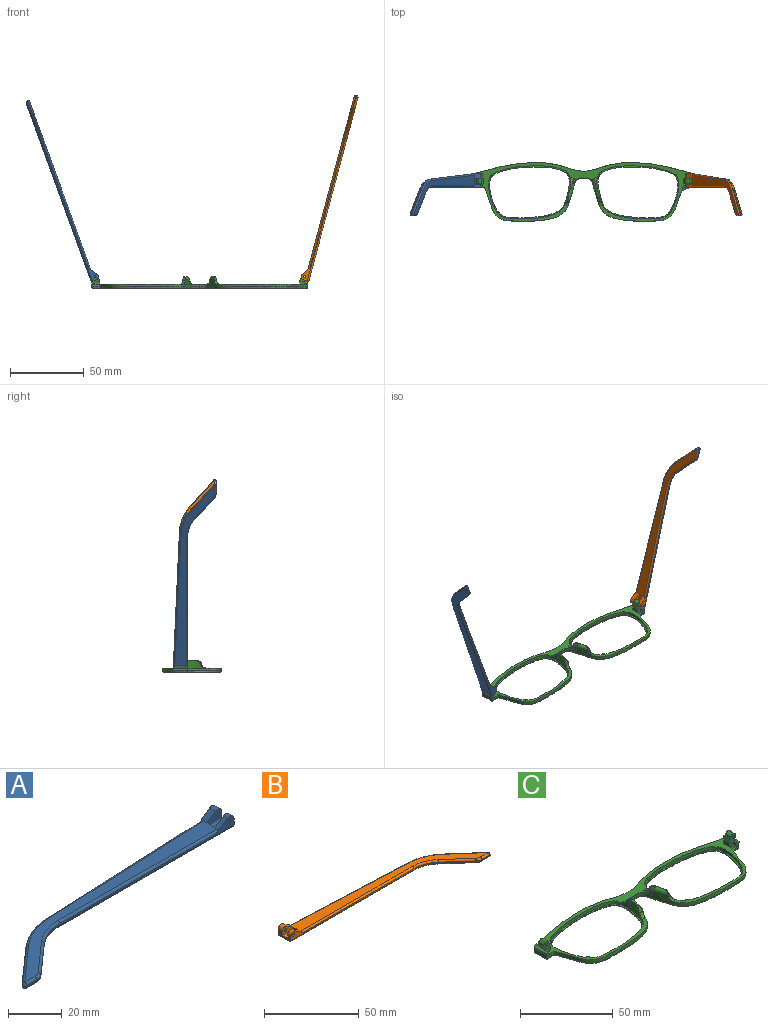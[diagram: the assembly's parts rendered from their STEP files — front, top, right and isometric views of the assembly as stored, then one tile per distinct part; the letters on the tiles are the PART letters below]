
ASSEMBLY  parts=3 mates=2
PART A: 43 faces, bbox 130.2x29.5x5.9 mm
  f0: plane 9.62x3.72mm, normal (1,0,0), area 24.7mm2, adj f1,f3,f4,f5,f10,f16,f18,f28
  f1: cylinder r=2.2mm len=3.45mm, axis (0,-1,0), area 11mm2, adj f0,f2,f4,f37
  f2: plane 6.01x3.91mm, normal (-0.55,0,0.84), area 12.7mm2, adj f1,f4,f9,f19,f37
  f3: plane 2.26x0.1mm, normal (0,0,1), area 0.1mm2, adj f0,f5,f18
  f4: plane 92.1x4.9mm, normal (0,-1,0), area 79.9mm2, adj f0,f1,f2,f14,f19,f36,f42
  f5: plane 93.42x4.13mm, normal (-0.04,1,0), area 64.8mm2, adj f0,f3,f11,f15,f17,f27,f28
  f6: plane 17.82x15.72mm, normal (-0.66,0.75,0), area 14.3mm2, adj f11,f12,f25,f30
  f7: plane 5.46x0.6mm, normal (0,-1,0), area 3.3mm2, adj f12,f13,f23,f32
  f8: plane 14.99x13.23mm, normal (0.66,-0.75,0), area 12mm2, adj f13,f14,f21,f34
  f9: plane 121.18x26.73mm, normal (0,0,1), area 627.7mm2, adj f2,f17,f19,f20,f21,f22,f23,f25
  f10: plane 129.1x27.08mm, normal (0,0,-1), area 686.5mm2, adj f0,f28,f29,f30,f32,f33,f34,f35
  f11: cylinder r=30mm len=18.52mm, axis (0,0,-1), area 12.2mm2, adj f5,f6,f26,f29
  f12: cylinder r=1mm len=1.75mm, axis (0,0,-1), area 1.5mm2, adj f6,f7,f24,f31
  f13: cylinder r=5mm len=3.31mm, axis (0,0,-1), area 2.2mm2, adj f7,f8,f22,f33
  f14: cylinder r=20mm len=13.23mm, axis (0,0,1), area 8.7mm2, adj f4,f8,f20,f35
  f15: plane 5.66x0.25mm, normal (0,0,-1), area 0.7mm2, adj f5,f17,f18
  f16: cylinder r=2.2mm len=3.45mm, axis (0,-1,0), area 14.8mm2, adj f0,f17,f18,f38
  f17: plane 6.01x3.91mm, normal (-0.55,0,0.84), area 16.9mm2, adj f5,f9,f15,f16,f18,f27,f38
  f18: plane 7.92x3.3mm, normal (0,1,0), area 15.9mm2, adj f0,f3,f15,f16,f17,f41
  f19: cylinder r=1mm len=84.18mm, axis (-1,0,0), area 131.4mm2, adj f2,f4,f9,f20
  f20: torus R=21mm, axis (0,0,1), area 23.1mm2, adj f9,f14,f19,f21
  f21: cylinder r=1mm len=15.65mm, axis (-0.75,-0.66,0), area 31.4mm2, adj f8,f9,f20,f22
  f22: torus R=4mm, axis (0,0,1), area 5.3mm2, adj f9,f13,f21,f23
  f23: cylinder r=1mm len=5.46mm, axis (-1,0,0), area 8.6mm2, adj f7,f9,f22,f24
  f24: sphere r=1mm, area 2.4mm2, adj f12,f23,f25
  f25: cylinder r=1mm len=18.48mm, axis (0.75,0.66,0), area 37.3mm2, adj f6,f9,f24,f26
  f26: torus R=29mm, axis (0,0,1), area 31.6mm2, adj f9,f11,f25,f27
  f27: cylinder r=1mm len=85.5mm, axis (1,0.04,0), area 133.5mm2, adj f5,f9,f17,f26
  f28: cylinder r=1mm len=93.46mm, axis (-1,-0.04,0), area 146.9mm2, adj f0,f5,f10,f29
  f29: torus R=29mm, axis (0,0,1), area 31.6mm2, adj f10,f11,f28,f30
  f30: cylinder r=1mm len=18.48mm, axis (-0.75,-0.66,0), area 37.3mm2, adj f6,f10,f29,f31
  f31: sphere r=1mm, area 2.4mm2, adj f12,f30,f32
  f32: cylinder r=1mm len=5.46mm, axis (1,0,0), area 8.6mm2, adj f7,f10,f31,f33
  f33: torus R=4mm, axis (0,0,1), area 5.3mm2, adj f10,f13,f32,f34
  f34: cylinder r=1mm len=15.65mm, axis (0.75,0.66,0), area 31.4mm2, adj f8,f10,f33,f35
  f35: torus R=21mm, axis (0,0,1), area 23.1mm2, adj f10,f14,f34,f36
  f36: cylinder r=1mm len=92.1mm, axis (1,0,0), area 144.7mm2, adj f0,f4,f10,f35
  f37: plane 7.92x4.7mm, normal (0,1,0), area 27mm2, adj f0,f1,f2,f39,f40,f42
  f38: plane 7.92x4.7mm, normal (0,-1,0), area 27mm2, adj f0,f16,f17,f39,f40,f41
  f39: plane 7.92x4.1mm, normal (0,0,1), area 32.5mm2, adj f0,f37,f38,f40
  f40: plane 4.1x1.4mm, normal (1,0,0), area 5.7mm2, adj f9,f37,f38,f39
  f41: cylinder r=0.5mm len=3.1mm, axis (0,-1,0), area 9.7mm2, adj f18,f38
  f42: cylinder r=0.5mm len=2.3mm, axis (0,-1,0), area 7.2mm2, adj f4,f37
PART B: 43 faces, bbox 130.2x29.5x5.9 mm
  f0: plane 9.62x3.72mm, normal (-1,0,0), area 24.7mm2, adj f1,f3,f4,f5,f10,f16,f18,f28
  f1: cylinder r=2.2mm len=3.45mm, axis (0,-1,0), area 11mm2, adj f0,f2,f4,f37
  f2: plane 6.01x3.91mm, normal (0.55,0,0.84), area 12.7mm2, adj f1,f4,f9,f19,f37
  f3: plane 2.26x0.1mm, normal (0,0,1), area 0.1mm2, adj f0,f5,f18
  f4: plane 92.1x4.9mm, normal (0,-1,0), area 78.2mm2, adj f0,f1,f2,f14,f19,f36,f42
  f5: plane 93.42x4.13mm, normal (0.04,1,0), area 64.8mm2, adj f0,f3,f11,f15,f17,f27,f28
  f6: plane 17.82x15.72mm, normal (0.66,0.75,0), area 14.3mm2, adj f11,f12,f25,f30
  f7: plane 5.46x0.6mm, normal (0,-1,0), area 3.3mm2, adj f12,f13,f23,f32
  f8: plane 14.99x13.23mm, normal (-0.66,-0.75,0), area 12mm2, adj f13,f14,f21,f34
  f9: plane 121.18x26.73mm, normal (0,0,1), area 627.7mm2, adj f2,f17,f19,f20,f21,f22,f23,f25
  f10: plane 129.1x27.08mm, normal (0,0,-1), area 686.5mm2, adj f0,f28,f29,f30,f32,f33,f34,f35
  f11: cylinder r=30mm len=18.52mm, axis (0,0,-1), area 12.2mm2, adj f5,f6,f26,f29
  f12: cylinder r=1mm len=1.75mm, axis (0,0,-1), area 1.5mm2, adj f6,f7,f24,f31
  f13: cylinder r=5mm len=3.31mm, axis (0,0,-1), area 2.2mm2, adj f7,f8,f22,f33
  f14: cylinder r=20mm len=13.23mm, axis (0,0,1), area 8.7mm2, adj f4,f8,f20,f35
  f15: plane 5.66x0.25mm, normal (0,0,-1), area 0.7mm2, adj f5,f17,f18
  f16: cylinder r=2.2mm len=3.45mm, axis (0,-1,0), area 14.8mm2, adj f0,f17,f18,f38
  f17: plane 6.01x3.91mm, normal (0.55,0,0.84), area 16.9mm2, adj f5,f9,f15,f16,f18,f27,f38
  f18: plane 7.92x3.3mm, normal (0,1,0), area 14.3mm2, adj f0,f3,f15,f16,f17,f41
  f19: cylinder r=1mm len=84.18mm, axis (1,0,0), area 131.4mm2, adj f2,f4,f9,f20
  f20: torus R=21mm, axis (0,0,1), area 23.1mm2, adj f9,f14,f19,f21
  f21: cylinder r=1mm len=15.65mm, axis (0.75,-0.66,0), area 31.4mm2, adj f8,f9,f20,f22
  f22: torus R=4mm, axis (0,0,1), area 5.3mm2, adj f9,f13,f21,f23
  f23: cylinder r=1mm len=5.46mm, axis (1,0,0), area 8.6mm2, adj f7,f9,f22,f24
  f24: sphere r=1mm, area 2.4mm2, adj f12,f23,f25
  f25: cylinder r=1mm len=18.48mm, axis (-0.75,0.66,0), area 37.3mm2, adj f6,f9,f24,f26
  f26: torus R=29mm, axis (0,0,1), area 31.6mm2, adj f9,f11,f25,f27
  f27: cylinder r=1mm len=85.5mm, axis (-1,0.04,0), area 133.5mm2, adj f5,f9,f17,f26
  f28: cylinder r=1mm len=93.46mm, axis (1,-0.04,0), area 146.9mm2, adj f0,f5,f10,f29
  f29: torus R=29mm, axis (0,0,1), area 31.6mm2, adj f10,f11,f28,f30
  f30: cylinder r=1mm len=18.48mm, axis (0.75,-0.66,0), area 37.3mm2, adj f6,f10,f29,f31
  f31: sphere r=1mm, area 2.4mm2, adj f12,f30,f32
  f32: cylinder r=1mm len=5.46mm, axis (-1,0,0), area 8.6mm2, adj f7,f10,f31,f33
  f33: torus R=4mm, axis (0,0,1), area 5.3mm2, adj f10,f13,f32,f34
  f34: cylinder r=1mm len=15.65mm, axis (-0.75,0.66,0), area 31.4mm2, adj f8,f10,f33,f35
  f35: torus R=21mm, axis (0,0,1), area 23.1mm2, adj f10,f14,f34,f36
  f36: cylinder r=1mm len=92.1mm, axis (-1,0,0), area 144.7mm2, adj f0,f4,f10,f35
  f37: plane 7.92x4.7mm, normal (0,1,0), area 25.4mm2, adj f0,f1,f2,f39,f40,f42
  f38: plane 7.92x4.7mm, normal (0,-1,0), area 25.4mm2, adj f0,f16,f17,f39,f40,f41
  f39: plane 7.92x4.1mm, normal (0,0,1), area 32.5mm2, adj f0,f37,f38,f40
  f40: plane 4.1x1.4mm, normal (-1,0,0), area 5.7mm2, adj f9,f37,f38,f39
  f41: cylinder r=0.88mm len=3.1mm, axis (0,-1,0), area 17mm2, adj f18,f38
  f42: cylinder r=0.88mm len=2.3mm, axis (0,-1,0), area 12.6mm2, adj f4,f37
PART C: 118 faces, bbox 148.1x40.9x17.9 mm
  f0: bspline ~1.82x1.22mm, area 0.7mm2, adj f2,f7,f36,f52
  f1: plane 147.39x40.16mm, normal (0,0,1), area 759mm2, adj f4,f5,f6,f7,f8,f18,f19,f22
  f2: bspline ~6.08x4.93mm, area 12.6mm2, adj f0,f7,f36,f41,f43,f52,f53
  f3: plane 4.46x1.45mm, normal (0,0,1), area 0.1mm2, adj f7,f37
  f4: plane 1.23x0.04mm, normal (0,0,1), area 0mm2, adj f1,f7,f21
  f5: plane 6.97x5.07mm, normal (0,1,0), area 22.7mm2, adj f1,f19,f20,f24,f26,f27,f29,f30
  f6: plane 3.2x2.36mm, normal (0,-1,0), area 5.7mm2, adj f1,f19,f25,f28
  f7: extruded ~73.26x39.84mm, area 292.7mm2, adj f0,f1,f2,f3,f4,f8,f10,f11
  f8: extruded ~35.39x5.69mm, area 72.2mm2, adj f1,f7,f15,f67
  f9: plane 144.78x37.85mm, normal (0,0,-1), area 478.1mm2, adj f10,f12,f14,f15,f16,f68,f70,f72
  f10: bspline ~73.27x30.39mm, area 161.7mm2, adj f7,f9,f11,f68
  f11: bspline ~1x1mm, area 0.8mm2, adj f7,f10,f12
  f12: bspline ~8.99x1.23mm, area 12.6mm2, adj f7,f9,f11,f13
  f13: bspline ~1.04x1mm, area 0.7mm2, adj f7,f12,f14
  f14: bspline ~45.86x8.59mm, area 59.8mm2, adj f7,f9,f13,f15
  f15: bspline ~37.01x6.7mm, area 56.6mm2, adj f8,f9,f14,f73
  f16: bspline ~56.15x36.68mm, area 237.6mm2, adj f9,f17
  f17: plane 56.03x36.25mm, normal (0,0,1), area 125.3mm2, adj f16,f18
  f18: extruded ~55.63x36.1mm, area 379.4mm2, adj f1,f17,f38,f39,f40,f41,f42,f43
  f19: plane 4x2.36mm, normal (-1,0,0), area 9.5mm2, adj f1,f5,f6,f20
  f20: plane 4x0.02mm, normal (0.34,0,0.94), area 0.1mm2, adj f5,f19,f27
  f21: plane 2.76x2.53mm, normal (0,-1,0), area 3.9mm2, adj f4,f25,f26,f34,f56
  f22: plane 7.67x1.6mm, normal (0.94,0,-0.34), area 13mm2, adj f1,f34,f35,f56
  f23: plane 2.1x1.69mm, normal (0,1,0), area 2.8mm2, adj f1,f24,f26,f35,f56
  f24: plane 3.3x2.1mm, normal (-1,0,0), area 6.9mm2, adj f1,f5,f23,f26
  f25: plane 2.35x2.1mm, normal (-1,0,0), area 4.9mm2, adj f1,f6,f21,f26,f28
  f26: plane 9.65x1.24mm, normal (0,0,1), area 8.2mm2, adj f5,f21,f23,f24,f25,f28,f29,f56
  f27: plane 4x3.31mm, normal (-0.94,0,0.34), area 14.1mm2, adj f5,f20,f28,f31
  f28: plane 5.77x5.06mm, normal (0,-1,0), area 17mm2, adj f6,f25,f26,f27,f29,f30,f31,f32
  f29: plane 4x2.21mm, normal (0.94,0,-0.34), area 9.4mm2, adj f5,f26,f28,f32
  f30: plane 4x0.01mm, normal (0.34,0,0.94), area 0mm2, adj f5,f28,f31,f32
  f31: cylinder r=1.98mm len=4mm, axis (0,1,0), area 12.4mm2, adj f5,f27,f28,f30
  f32: cylinder r=1.98mm len=4mm, axis (0,-1,0), area 12.4mm2, adj f5,f28,f29,f30
  f33: cylinder r=0.88mm len=4mm, axis (0,-1,0), area 22mm2, adj f5,f28
  f34: cone r=1mm half-angle=20deg, axis (0,0,1), area 2.3mm2, adj f1,f21,f22,f56
  f35: cylinder r=1mm len=2.28mm, axis (-0.34,0,-0.94), area 3mm2, adj f1,f22,f23,f56
  f36: extruded ~3.67x3.12mm, area 6mm2, adj f0,f2,f7,f59
  f37: extruded ~4.44x3.32mm, area 15.1mm2, adj f3,f7,f42,f43,f55
  f38: extruded ~4.98x1.7mm, area 8mm2, adj f18,f41
  f39: extruded ~0.3x0.06mm, area 0mm2, adj f18
  f40: plane 3.64x0.97mm, normal (0,0,1), area 0.3mm2, adj f18,f41,f43
  f41: bspline ~15.5x15.35mm, area 6.5mm2, adj f2,f18,f38,f40,f54
  f42: bspline ~7.26x7.26mm, area 6.3mm2, adj f18,f37,f43,f55
  f43: bspline ~10.82x4.98mm, area 21.5mm2, adj f2,f7,f18,f37,f40,f42
  f44: cylinder r=2.28mm len=2.86mm, axis (0,0,1), area 1.8mm2, adj f1,f18,f45,f54
  f45: plane 2.88x1.51mm, normal (0,0,-1), area 1.8mm2, adj f18,f44
  f46: cylinder r=2.28mm len=2.47mm, axis (0,0,1), area 1.7mm2, adj f1,f18,f47
  f47: plane 2.5x1.83mm, normal (0,0,-1), area 1.7mm2, adj f18,f46
  f48: cylinder r=1.3mm len=1.78mm, axis (0,0,1), area 1.3mm2, adj f1,f18,f49
  f49: plane 1.79x1.31mm, normal (0,0,-1), area 0.9mm2, adj f18,f48
  f50: cylinder r=1.3mm len=1.93mm, axis (0,0,1), area 1.5mm2, adj f1,f18,f51
  f51: plane 1.95x1.68mm, normal (0,0,-1), area 1.5mm2, adj f18,f50
  f52: bspline ~2.67x2.04mm, area 1.9mm2, adj f0,f2,f7,f53,f58
  f53: bspline ~3.55x3.47mm, area 3.7mm2, adj f1,f2,f52,f54,f58
  f54: bspline ~6.14x4.44mm, area 7.6mm2, adj f1,f18,f41,f44,f53
  f55: bspline ~3.7x3.66mm, area 7.8mm2, adj f1,f7,f18,f37,f42
  f56: plane 9.71x1.44mm, normal (0.34,0,0.94), area 13.9mm2, adj f21,f22,f23,f26,f34,f35
  f57: bspline ~6.38x2.14mm, area 2.6mm2, adj f1,f7,f58,f115
  f58: bspline ~2.1x1.46mm, area 0.6mm2, adj f7,f52,f53,f57
  f59: bspline ~5.24x1.75mm, area 0mm2, adj f7,f36
  f60: bspline ~2.19x1.4mm, area 0.7mm2, adj f61,f66,f94,f110
  f61: bspline ~6.08x4.93mm, area 12.6mm2, adj f60,f66,f94,f99,f101,f110,f111
  f62: plane 4.46x1.45mm, normal (0,0,1), area 0.1mm2, adj f66,f95
  f63: plane 1.23x0.04mm, normal (0,0,1), area 0mm2, adj f1,f66,f79
  f64: plane 6.97x5.07mm, normal (0,1,0), area 22.7mm2, adj f1,f77,f78,f82,f84,f85,f87,f88
  f65: plane 3.2x2.36mm, normal (0,-1,0), area 5.7mm2, adj f1,f77,f83,f86
  f66: extruded ~73.26x39.84mm, area 292.7mm2, adj f1,f7,f60,f61,f62,f63,f67,f68
  f67: extruded ~35.39x5.69mm, area 72.2mm2, adj f1,f8,f66,f73
  f68: bspline ~73.83x30.39mm, area 161.7mm2, adj f9,f10,f66,f69
  f69: bspline ~1x1mm, area 0.8mm2, adj f66,f68,f70
  f70: bspline ~8.99x1.23mm, area 12.6mm2, adj f9,f66,f69,f71
  f71: bspline ~1.04x1mm, area 0.8mm2, adj f66,f70,f72
  f72: bspline ~45.86x8.59mm, area 59.8mm2, adj f9,f66,f71,f73
  f73: bspline ~37.01x6.7mm, area 56.6mm2, adj f9,f15,f67,f72
  f74: bspline ~56.15x36.68mm, area 237.6mm2, adj f9,f75
  f75: plane 56.03x36.25mm, normal (0,0,1), area 125.3mm2, adj f74,f76
  f76: extruded ~55.63x36.1mm, area 379.4mm2, adj f1,f75,f96,f97,f98,f99,f100,f101
  f77: plane 4x2.36mm, normal (1,0,0), area 9.5mm2, adj f1,f64,f65,f78
  f78: plane 4x0.02mm, normal (-0.34,0,0.94), area 0.1mm2, adj f64,f77,f85
  f79: plane 2.76x2.53mm, normal (0,-1,0), area 3.9mm2, adj f63,f83,f84,f92,f114
  f80: plane 7.67x1.6mm, normal (-0.94,0,-0.34), area 13mm2, adj f1,f92,f93,f114
  f81: plane 2.1x1.69mm, normal (0,1,0), area 2.8mm2, adj f1,f82,f84,f93,f114
  f82: plane 3.3x2.1mm, normal (1,0,0), area 6.9mm2, adj f1,f64,f81,f84
  f83: plane 2.35x2.1mm, normal (1,0,0), area 4.9mm2, adj f1,f65,f79,f84,f86
  f84: plane 9.65x1.24mm, normal (0,0,1), area 8.2mm2, adj f64,f79,f81,f82,f83,f86,f87,f114
  f85: plane 4x3.31mm, normal (0.94,0,0.34), area 14.1mm2, adj f64,f78,f86,f89
  f86: plane 5.77x5.06mm, normal (0,-1,0), area 17mm2, adj f65,f83,f84,f85,f87,f88,f89,f90
  f87: plane 4x2.21mm, normal (-0.94,0,-0.34), area 9.4mm2, adj f64,f84,f86,f90
  f88: plane 4x0.01mm, normal (-0.34,0,0.94), area 0mm2, adj f64,f86,f89,f90
  f89: cylinder r=1.98mm len=4mm, axis (0,1,0), area 12.4mm2, adj f64,f85,f86,f88
  f90: cylinder r=1.98mm len=4mm, axis (0,-1,0), area 12.4mm2, adj f64,f86,f87,f88
  f91: cylinder r=0.88mm len=4mm, axis (0,-1,0), area 22mm2, adj f64,f86
  f92: cone r=1mm half-angle=20deg, axis (0,0,1), area 2.3mm2, adj f1,f79,f80,f114
  f93: cylinder r=1mm len=2.28mm, axis (0.34,0,-0.94), area 3mm2, adj f1,f80,f81,f114
  f94: extruded ~3.67x3.12mm, area 6mm2, adj f60,f61,f66,f117
  f95: extruded ~4.44x3.32mm, area 15.1mm2, adj f62,f66,f100,f101,f113
  f96: extruded ~4.98x1.7mm, area 8mm2, adj f76,f99
  f97: extruded ~0.3x0.06mm, area 0mm2, adj f76
  f98: plane 3.64x0.97mm, normal (0,0,1), area 0.3mm2, adj f76,f99,f101
  f99: bspline ~15.5x15.35mm, area 6.4mm2, adj f61,f76,f96,f98,f112
  f100: bspline ~7.26x7.26mm, area 6.2mm2, adj f76,f95,f101,f113
  f101: bspline ~9.7x4.68mm, area 21.5mm2, adj f61,f66,f76,f95,f98,f100
  f102: cylinder r=2.28mm len=2.86mm, axis (0,0,1), area 1.8mm2, adj f1,f76,f103,f112
  f103: plane 2.88x1.51mm, normal (0,0,-1), area 1.8mm2, adj f76,f102
  f104: cylinder r=2.28mm len=2.47mm, axis (0,0,1), area 1.7mm2, adj f1,f76,f105
  f105: plane 2.5x1.83mm, normal (0,0,-1), area 1.7mm2, adj f76,f104
  f106: cylinder r=1.3mm len=1.78mm, axis (0,0,1), area 1.3mm2, adj f1,f76,f107
  f107: plane 1.79x1.31mm, normal (0,0,-1), area 0.9mm2, adj f76,f106
  f108: cylinder r=1.3mm len=1.93mm, axis (0,0,1), area 1.5mm2, adj f1,f76,f109
  f109: plane 1.95x1.68mm, normal (0,0,-1), area 1.5mm2, adj f76,f108
  f110: bspline ~2.66x2.04mm, area 1.9mm2, adj f60,f61,f66,f111,f116
  f111: bspline ~3.55x3.47mm, area 3.7mm2, adj f1,f61,f110,f112,f116
  f112: bspline ~5.92x4.42mm, area 7.6mm2, adj f1,f76,f99,f102,f111
  f113: bspline ~3.7x3.66mm, area 7.8mm2, adj f1,f66,f76,f95,f100
  f114: plane 9.71x1.44mm, normal (-0.34,0,0.94), area 13.9mm2, adj f79,f80,f81,f84,f92,f93
  f115: bspline ~6.38x2.14mm, area 2.6mm2, adj f1,f57,f66,f116
  f116: bspline ~2.1x1.46mm, area 0.6mm2, adj f66,f110,f111,f115
  f117: bspline ~5.24x1.75mm, area 0mm2, adj f66,f94
PLACE A rot(axis=(0,1,0),70deg) t=(-84.77,-5.75,56)mm
PLACE B rot(axis=(0,-1,0),75deg) t=(68.2,-5.75,-61.61)mm
PLACE C t=(10.15,-1.13,-5.77)mm
MATE revolute A.f1 <-> C.f89  axis (0,-1,0) through (-60.89,2.72,1.22)mm
MATE revolute B.f41 <-> C.f32  axis (0,-1,0) through (81.2,2.72,1.21)mm
